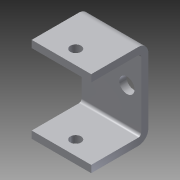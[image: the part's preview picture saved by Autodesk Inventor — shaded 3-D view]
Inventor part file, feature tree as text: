
AUTODESK INVENTOR PART (.ipt)
format: ipt  version: 2013 (Build 170138000, 138)  size: 132,608 bytes
history: native  units: in
note: dims shown in document units (in); Inventor stores cm internally (conversion verified against a paired STEP export)
features: sheet_metal_op x4, sketch x4, other x3, reference x2, extrude x1
ambient origin geometry x8: Origin, YZ Plane, XZ Plane, XY Plane, X Axis, Y Axis, Z Axis, Center Point
bodies: Solid1 (feature_tree)
feature tree (14):
  sheet_metal_op  "Face1"
  sheet_metal_op  "Flange1"
  extrude  "Extrusion1"  Depth=1.15in
  sketch  "Sketch1"  dims[d4=0.5788in d5=1.15in]
  other  "Plate1"
  sketch  "Sketch2"  dims[d6=0.125in]
  other  "Plate2"
  sheet_metal_op  "Bend1"
  sheet_metal_op  "Corner1"
  sketch  "Sketch3"  dims[d7=0.125in]
  sketch  "Sketch5"  dims[d8=0.0625in d9=0.25in d10=0.125in d11=1.0in d12=90.0deg d13=0.05in d14=0.5in d15=0.125in d16=0.125in d17=0.25in d18=0.1875in d19=2999.0in d20=0.0in d21=0.575in d22=0.125in d23=0.0in]
  reference  "Reference1"
  reference  "Reference2"
  other  "Cut1"
